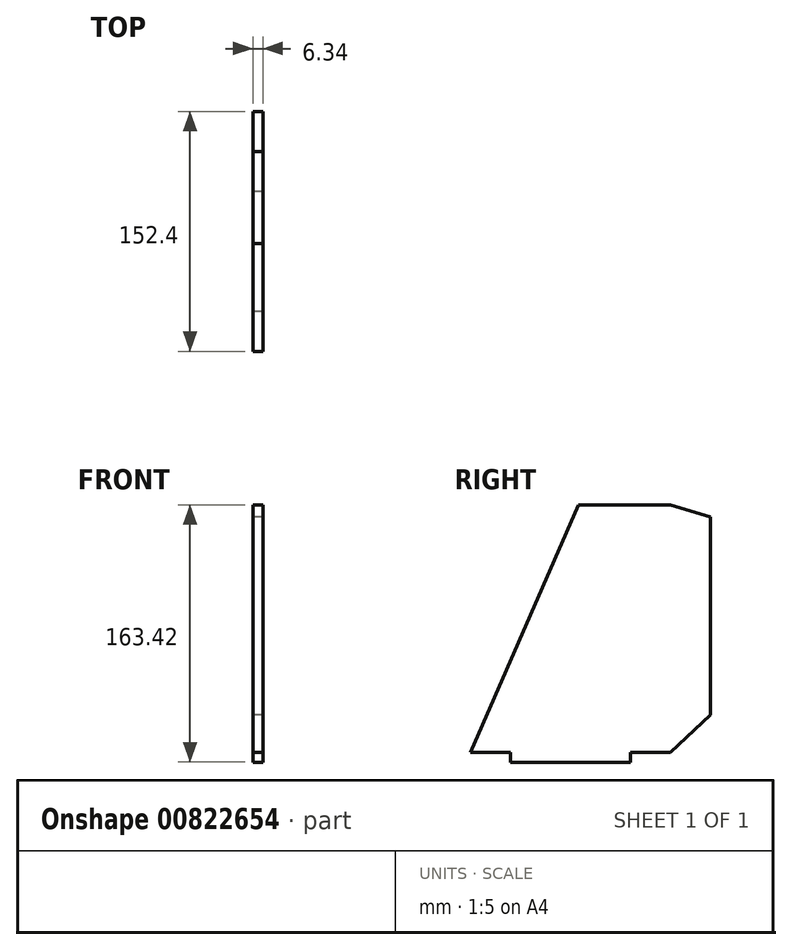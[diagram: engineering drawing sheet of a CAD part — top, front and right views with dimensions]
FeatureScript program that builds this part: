
annotation { "Feature Type Name" : "Feature", "Feature Type Description" : "" }
export const myFeature = defineFeature(function(context is Context, id is Id, definition is map)
    precondition{}
    {
        {
            var Q0;
            Q0=qCreatedBy(makeId("Right.planeOp"),FACE);
            var sketch = newSketch(context, id + "F0", { "sketchPlane" : qUnion([Q0])});
            skLineSegment(sketch, "E0", {"start": v(0, -58.58) * mm, "end": v(-50.8, -58.58) * mm});
            skLineSegment(sketch, "E1", {"start": v(-50.8, -58.58) * mm, "end": v(17.83, 98.49) * mm});
            skLineSegment(sketch, "E2", {"start": v(17.83, 98.49) * mm, "end": v(76.2, 98.49) * mm});
            skLineSegment(sketch, "E3", {"start": v(76.2, 98.49) * mm, "end": v(101.6, 90.7) * mm});
            skLineSegment(sketch, "E4", {"start": v(101.6, 90.7) * mm, "end": v(101.6, -34.88) * mm});
            skLineSegment(sketch, "E5", {"start": v(101.6, -34.88) * mm, "end": v(76.2, -58.58) * mm});
            skLineSegment(sketch, "E6", {"start": v(76.2, -58.58) * mm, "end": v(0, -58.58) * mm});
            skLineSegment(sketch, "E7", {"start": v(-25.4, -58.58) * mm, "end": v(-25.4, -64.93) * mm});
            skLineSegment(sketch, "E8", {"start": v(-25.4, -64.93) * mm, "end": v(50.8, -64.93) * mm});
            skLineSegment(sketch, "E9", {"start": v(50.8, -64.93) * mm, "end": v(50.8, -58.58) * mm});
            skSolve(sketch);
        }
        {
            var Q0;
            Q0 = qSketchRegion(id + "F0", true);
            extrude(context, id + "F1", {"entities" : qUnion([Q0]), "endBound" : BoundingType.SYMMETRIC, "depth" : 6.35 * mm, "offsetDistance" : 25.4 * mm});
        }
    });
